# Revit family: 32QMC_231217_1
name_source: partatom
category: 통신 장치
units: mm (PartAtom-declared; Revit-internal decimal feet)

## family parameters
OmniClass 번호 = 23.85.10.14.24
OmniClass 제목 = Video Monitors
공유 = 아니오
로드될 때 보이드를 사용하여 절단 = 아니오
룸 계산 점 = 아니오
부품 유형 = 보통
원형 커넥터 치수 = 지름 사용
작업 기준면 기반 = 아니오
주석 방향을 유지합니다. = 아니오
항상 수직 = 예

## types (1)
- UHD Signage QM32C
    Active Display Area = 698.4(H) x 392.85(V)
    Bezel Width (mm) = 11.5  [stored 0.0377297 ft]
    Brightness (Typ.) = 400 nit
    Color Gamut = NTSC 72%
    Contrast Ratio (Typ.) = 4,000:1(*IPS-1200:1)
    Diagonal Size (Class) = 32  [stored 0.104987 ft]
    Diagonal Size (Measured) = 31.5
    Dimension Package (mm) = 817 x 507 x 119
    Dimension Set (mm) = 727.3 x 421.9 x 28.5
    Dimension Set Depth (mm) = 28.5  [stored 0.0935039 ft]
    Dimension Set Height (mm) = 421.9  [stored 1.38419 ft]
    Dimension Set Width (mm) = 727.3  [stored 2.38615 ft]
    EMC = Class B
    Environment = ENERGY STAR 8.0, EPEAT
    External Control = RS232C(In/Out),RJ45
    Haze = 2%
    IP Rating = IP5x
    Input USB = USB 2.0 x 2
    Input Video = HDMI 2.0(3)
    Internal Operating System = Tizen 7.0
    Internal Processor = CA53 1.3GHz Quad-Core
    Internal Storage (FDM) = 8GB (3GB available)
    Key = UHD Signage with Built-in MagicInfoS10, SSSP10.0
    Operation Hour = 24/7
    Optional Specialty = TBD
    Optional Stand = STN-L3200C
    Orientation = Landscape/Portrait
    Output Audio = Stereo mini Jack
    Pixel Pitch (mm) = 0.360(H) x 0.360(V)
    Power Consumption Max [W/h] = 55
    Power Consumption Sleep mode = less than 0.5W
    Power Consumption Typical [W/h] = 29
    Power Supply = AC100 - 240V, 50/60 Hz
    Relative Humidity = 10~80%
    Resolution = 1920 x 1080 (16:9)
    Safety = 60950-1/62368-1
    Screen = Samsung Electronics Screen
    Security = 802.1 x (WPA2 Enterprise) : EAP-TLS, EAP-TTLS, EAP-PEAP
    Speaker = 10W 2ch
    Temperature = 0℃ ~ 40℃
    Type = VA/IPS
    VESA Mount = 100 x 100
    VESA Mount Screw (Min-Max) = M4, 10-12mm
    Weight Package (kg) = 6.9
    Weight Set (kg) = 5.2
    WiFi/BT = O/O
    모델 = UHD Signage QM32C
    제조업체 = Samsung Electronics Co., Ltd.
    조합 코드 = E1020500
    키노트 = 11 52 00

note: [stored X ft] marks values corroborated as IEEE doubles in the binary element streams (Revit-internal decimal feet)
